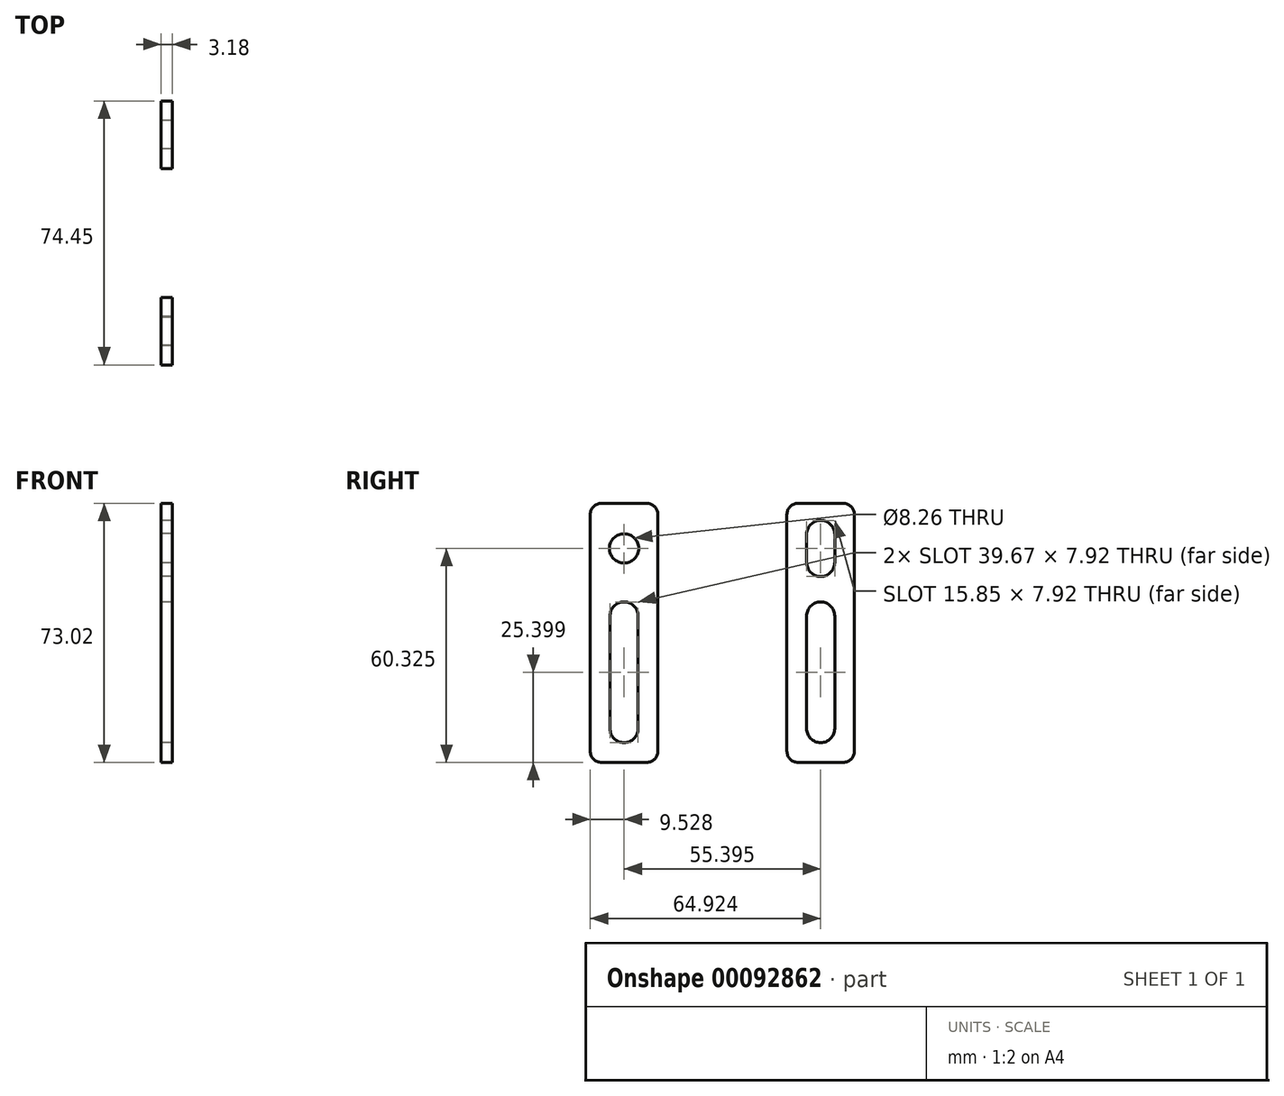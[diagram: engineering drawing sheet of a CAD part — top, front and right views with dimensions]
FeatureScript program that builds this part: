
annotation { "Feature Type Name" : "Feature", "Feature Type Description" : "" }
export const myFeature = defineFeature(function(context is Context, id is Id, definition is map)
    precondition{}
    {
        {
            var Q0;
            Q0=qCreatedBy(makeId("Right.planeOp"),FACE);
            var sketch = newSketch(context, id + "F0", { "sketchPlane" : qUnion([Q0])});
            skLineSegment(sketch, "E0.bottom", {"start": v(-45.02, 50.1) * mm, "end": v(-25.97, 50.1) * mm});
            skLineSegment(sketch, "E0.top", {"start": v(-45.02, -22.93) * mm, "end": v(-25.97, -22.93) * mm});
            skLineSegment(sketch, "E0.left", {"start": v(-45.02, 50.1) * mm, "end": v(-45.02, -22.93) * mm});
            skLineSegment(sketch, "E0.right", {"start": v(-25.97, 50.1) * mm, "end": v(-25.97, -22.93) * mm});
            skLineSegment(sketch, "E1.bottom", {"start": v(10.38, 50.1) * mm, "end": v(29.43, 50.1) * mm});
            skLineSegment(sketch, "E1.top", {"start": v(10.38, -22.93) * mm, "end": v(29.43, -22.93) * mm});
            skLineSegment(sketch, "E1.left", {"start": v(10.38, 50.1) * mm, "end": v(10.38, -22.93) * mm});
            skLineSegment(sketch, "E1.right", {"start": v(29.43, 50.1) * mm, "end": v(29.43, -22.93) * mm});
            skLineSegment(sketch, "E2", {"start": v(-45.02, -13.4) * mm, "end": v(29.43, -13.4) * mm, "construction": true});
            skLineSegment(sketch, "E3", {"start": v(-45.02, 18.34) * mm, "end": v(29.43, 18.34) * mm, "construction": true});
            skLineSegment(sketch, "E4", {"start": v(-45.02, 37.4) * mm, "end": v(29.43, 37.4) * mm, "construction": true});
            skLineSegment(sketch, "E5", {"start": v(-35.5, 50.1) * mm, "end": v(-35.5, -22.93) * mm, "construction": true});
            skLineSegment(sketch, "E6", {"start": v(19.9, 50.1) * mm, "end": v(19.9, -22.93) * mm, "construction": true});
            skLineSegment(sketch, "E7", {"start": v(-35.5, 18.34) * mm, "end": v(-35.5, -13.4) * mm});
            skLineSegment(sketch, "E8", {"start": v(19.9, 18.34) * mm, "end": v(19.9, -13.4) * mm});
            skLineSegment(sketch, "E9", {"start": v(10.38, 41.36) * mm, "end": v(29.43, 41.36) * mm, "construction": true});
            skLineSegment(sketch, "E10", {"start": v(10.38, 33.43) * mm, "end": v(29.43, 33.43) * mm, "construction": true});
            skLineSegment(sketch, "E11", {"start": v(19.9, 41.36) * mm, "end": v(19.9, 33.43) * mm});
            skCircle(sketch, "E12", {"center": v(-35.5, 37.4) * mm, "radius": 4.13 * mm});
            skArc(sketch, "E13.0.startCap", {"start": v(-39.45, 18.34) * mm, "mid": v(-35.5, 22.3) * mm, "end": v(-31.53, 18.34) * mm});
            skArc(sketch, "E13.0.endCap", {"start": v(-31.53, -13.4) * mm, "mid": v(-35.5, -17.37) * mm, "end": v(-39.45, -13.4) * mm});
            skLineSegment(sketch, "E13.0.left", {"start": v(-31.53, 18.34) * mm, "end": v(-31.53, -13.4) * mm});
            skLineSegment(sketch, "E13.0.right", {"start": v(-39.45, 18.34) * mm, "end": v(-39.45, -13.4) * mm});
            skArc(sketch, "E13.1.startCap", {"start": v(15.94, 41.36) * mm, "mid": v(19.9, 45.32) * mm, "end": v(23.87, 41.36) * mm});
            skArc(sketch, "E13.1.endCap", {"start": v(23.87, 33.43) * mm, "mid": v(19.9, 29.47) * mm, "end": v(15.94, 33.43) * mm});
            skLineSegment(sketch, "E13.1.left", {"start": v(23.87, 41.36) * mm, "end": v(23.87, 33.43) * mm});
            skLineSegment(sketch, "E13.1.right", {"start": v(15.94, 41.36) * mm, "end": v(15.94, 33.43) * mm});
            skArc(sketch, "E13.2.startCap", {"start": v(15.94, 18.34) * mm, "mid": v(19.9, 22.3) * mm, "end": v(23.87, 18.34) * mm});
            skArc(sketch, "E13.2.endCap", {"start": v(23.87, -13.4) * mm, "mid": v(19.9, -17.37) * mm, "end": v(15.94, -13.4) * mm});
            skLineSegment(sketch, "E13.2.left", {"start": v(23.87, 18.34) * mm, "end": v(23.87, -13.4) * mm});
            skLineSegment(sketch, "E13.2.right", {"start": v(15.94, 18.34) * mm, "end": v(15.94, -13.4) * mm});
            skSolve(sketch);
        }
        {
            var Q0;
            Q0=makeQuery(id+"F0.imprint","IMPRINT",FACE,{"disambiguationData":[TD([[makeQuery(id+"F0.imprint","IMPRINT",EDGE,{"derivedFrom":sQuery(id+"F0.wireOp",EDGE,"E0.bottom")}),-1.0]])]});
            var Q1;
            Q1=makeQuery(id+"F0.imprint","IMPRINT",FACE,{"disambiguationData":[TD([[makeQuery(id+"F0.imprint","IMPRINT",EDGE,{"derivedFrom":sQuery(id+"F0.wireOp",EDGE,"E1.bottom")}),-1.0]])]});
            extrude(context, id + "F1", {"entities" : qUnion([Q0, Q1]), "depth" : 3.17 * mm});
        }
        {
            var Q0;
            Q0=makeQuery(id+"F1.opExtrude","SWEPT_EDGE",EDGE,{"disambiguationData":[OSD([sQuery(id+"F0.wireOp",EDGE,"E0.bottom"),sQuery(id+"F0.wireOp",EDGE,"E0.left")])]});
            var Q1;
            Q1=makeQuery(id+"F1.opExtrude","SWEPT_EDGE",EDGE,{"disambiguationData":[OSD([sQuery(id+"F0.wireOp",EDGE,"E0.bottom"),sQuery(id+"F0.wireOp",EDGE,"E0.right")])]});
            var Q2;
            Q2=makeQuery(id+"F1.opExtrude","SWEPT_EDGE",EDGE,{"disambiguationData":[OSD([sQuery(id+"F0.wireOp",EDGE,"E1.bottom"),sQuery(id+"F0.wireOp",EDGE,"E1.left")])]});
            var Q3;
            Q3=makeQuery(id+"F1.opExtrude","SWEPT_EDGE",EDGE,{"disambiguationData":[OSD([sQuery(id+"F0.wireOp",EDGE,"E1.bottom"),sQuery(id+"F0.wireOp",EDGE,"E1.right")])]});
            var Q4;
            Q4=makeQuery(id+"F1.opExtrude","SWEPT_EDGE",EDGE,{"disambiguationData":[OSD([sQuery(id+"F0.wireOp",EDGE,"E0.top"),sQuery(id+"F0.wireOp",EDGE,"E0.left")])]});
            var Q5;
            Q5=makeQuery(id+"F1.opExtrude","SWEPT_EDGE",EDGE,{"disambiguationData":[OSD([sQuery(id+"F0.wireOp",EDGE,"E0.top"),sQuery(id+"F0.wireOp",EDGE,"E0.right")])]});
            var Q6;
            Q6=makeQuery(id+"F1.opExtrude","SWEPT_EDGE",EDGE,{"disambiguationData":[OSD([sQuery(id+"F0.wireOp",EDGE,"E1.top"),sQuery(id+"F0.wireOp",EDGE,"E1.left")])]});
            var Q7;
            Q7=makeQuery(id+"F1.opExtrude","SWEPT_EDGE",EDGE,{"disambiguationData":[OSD([sQuery(id+"F0.wireOp",EDGE,"E1.top"),sQuery(id+"F0.wireOp",EDGE,"E1.right")])]});
            fillet(context, id + "F2", {"entities" : qUnion([Q0, Q1, Q2, Q3, Q4, Q5, Q6, Q7]), "radius" : 3.17 * mm, "tangentPropagation" : true, "allowEdgeOverflow" : false});
        }
    });
